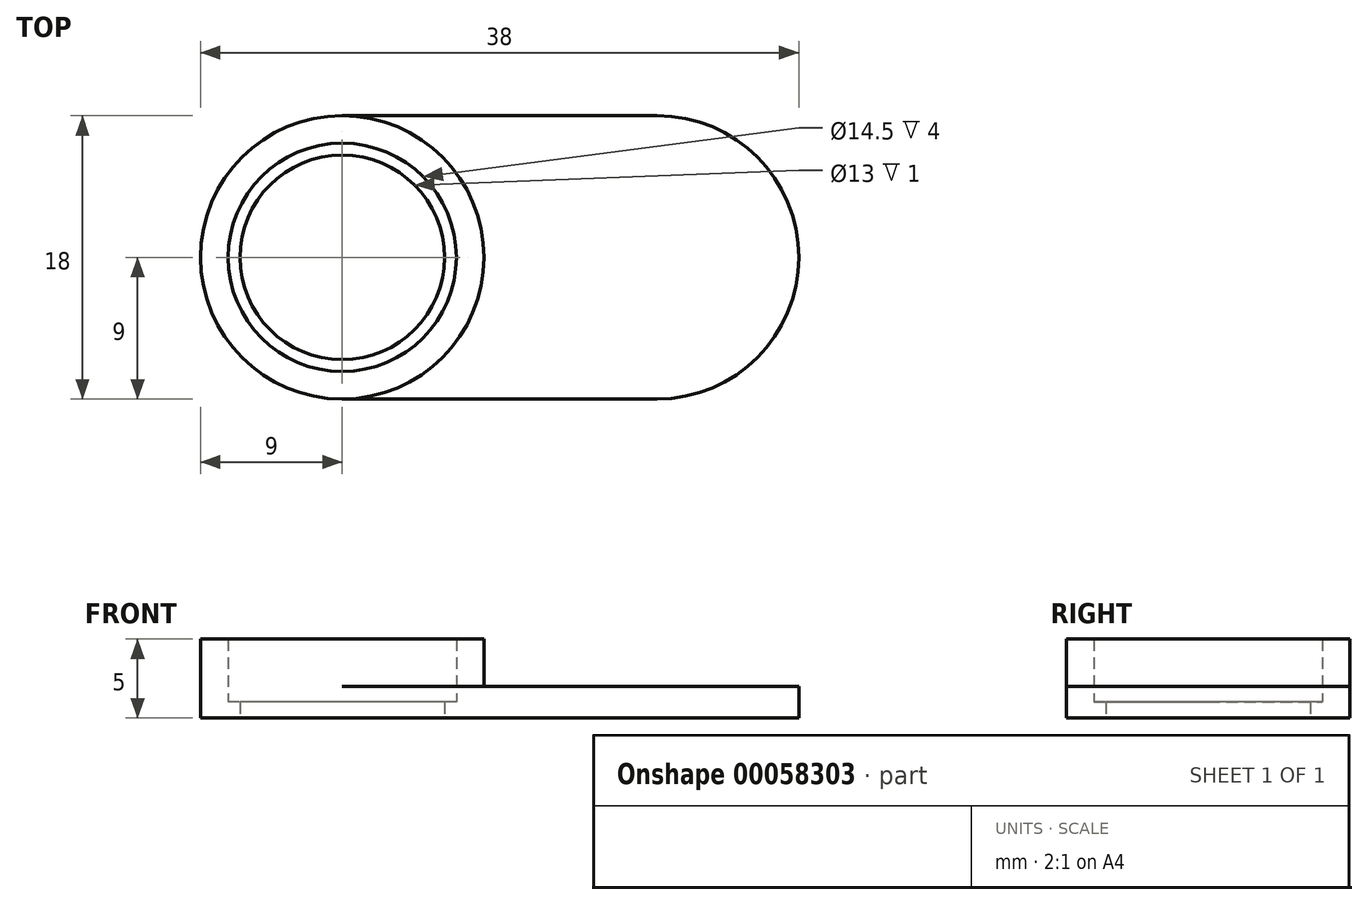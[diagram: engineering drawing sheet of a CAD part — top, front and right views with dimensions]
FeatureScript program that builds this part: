
annotation { "Feature Type Name" : "Feature", "Feature Type Description" : "" }
export const myFeature = defineFeature(function(context is Context, id is Id, definition is map)
    precondition{}
    {
        {
            var Q0;
            Q0=qCreatedBy(makeId("Top.planeOp"),FACE);
            var sketch = newSketch(context, id + "F0", { "sketchPlane" : qUnion([Q0])});
            skCircle(sketch, "E0", {"center": v(0, 0) * mm, "radius": 6.5 * mm});
            skCircle(sketch, "E1", {"center": v(0, 0) * mm, "radius": 7.25 * mm});
            skArc(sketch, "E2", {"start": v(0, 9) * mm, "mid": v(-9, 0) * mm, "end": v(0, -9) * mm});
            skArc(sketch, "E3", {"start": v(20, -9) * mm, "mid": v(29, 0) * mm, "end": v(20, 9) * mm});
            skLineSegment(sketch, "E4", {"start": v(0, 9) * mm, "end": v(20, 9) * mm});
            skLineSegment(sketch, "E5", {"start": v(0, -9) * mm, "end": v(20, -9) * mm});
            skSolve(sketch);
        }
        {
            var Q0;
            Q0=makeQuery(id+"F0.imprint","IMPRINT",FACE,{"disambiguationData":[TD([[makeQuery(id+"F0.imprint","IMPRINT",EDGE,{"derivedFrom":sQuery(id+"F0.wireOp",EDGE,"E1")}),-1.0]])]});
            extrude(context, id + "F1", {"entities" : qUnion([Q0]), "depth" : 5 * mm});
        }
        {
            var Q0;
            Q0=makeQuery(id+"F0.imprint","IMPRINT",FACE,{"disambiguationData":[TD([[makeQuery(id+"F0.imprint","IMPRINT",EDGE,{"derivedFrom":sQuery(id+"F0.wireOp",EDGE,"E0")}),-1.0]])]});
            extrude(context, id + "F2", {"entities" : qUnion([Q0]), "operationType" : NewBodyOperationType.ADD, "depth" : 1 * mm});
        }
        {
            var Q0;
            Q0=makeQuery(id+"F1.opExtrude","CAP_FACE",FACE,{"disambiguationData":[OSD([sQuery(id+"F0.wireOp",EDGE,"E1"),sQuery(id+"F0.wireOp",EDGE,"E2"),sQuery(id+"F0.wireOp",EDGE,"E3"),sQuery(id+"F0.wireOp",EDGE,"E4"),sQuery(id+"F0.wireOp",EDGE,"E5")])],"isStart":false});
            var sketch = newSketch(context, id + "F3", { "sketchPlane" : qUnion([Q0])});
            skArc(sketch, "E6", {"start": v(0, -9) * mm, "mid": v(9, 0) * mm, "end": v(0, 9) * mm});
            skArc(sketch, "E7", {"start": v(20, -9) * mm, "mid": v(29, 0) * mm, "end": v(20, 9) * mm});
            skLineSegment(sketch, "E8", {"start": v(0, 9) * mm, "end": v(20, 9) * mm});
            skLineSegment(sketch, "E9", {"start": v(0, -9) * mm, "end": v(20, -9) * mm});
            skSolve(sketch);
        }
        {
            var Q0;
            Q0=makeQuery(id+"F3.imprint","IMPRINT",FACE,{"disambiguationData":[TD([[makeQuery(id+"F3.imprint","IMPRINT",EDGE,{"derivedFrom":sQuery(id+"F3.wireOp",EDGE,"E6")}),-1.0]])]});
            extrude(context, id + "F4", {"entities" : qUnion([Q0]), "operationType" : NewBodyOperationType.REMOVE, "oppositeDirection" : true, "depth" : 3 * mm});
        }
    });
